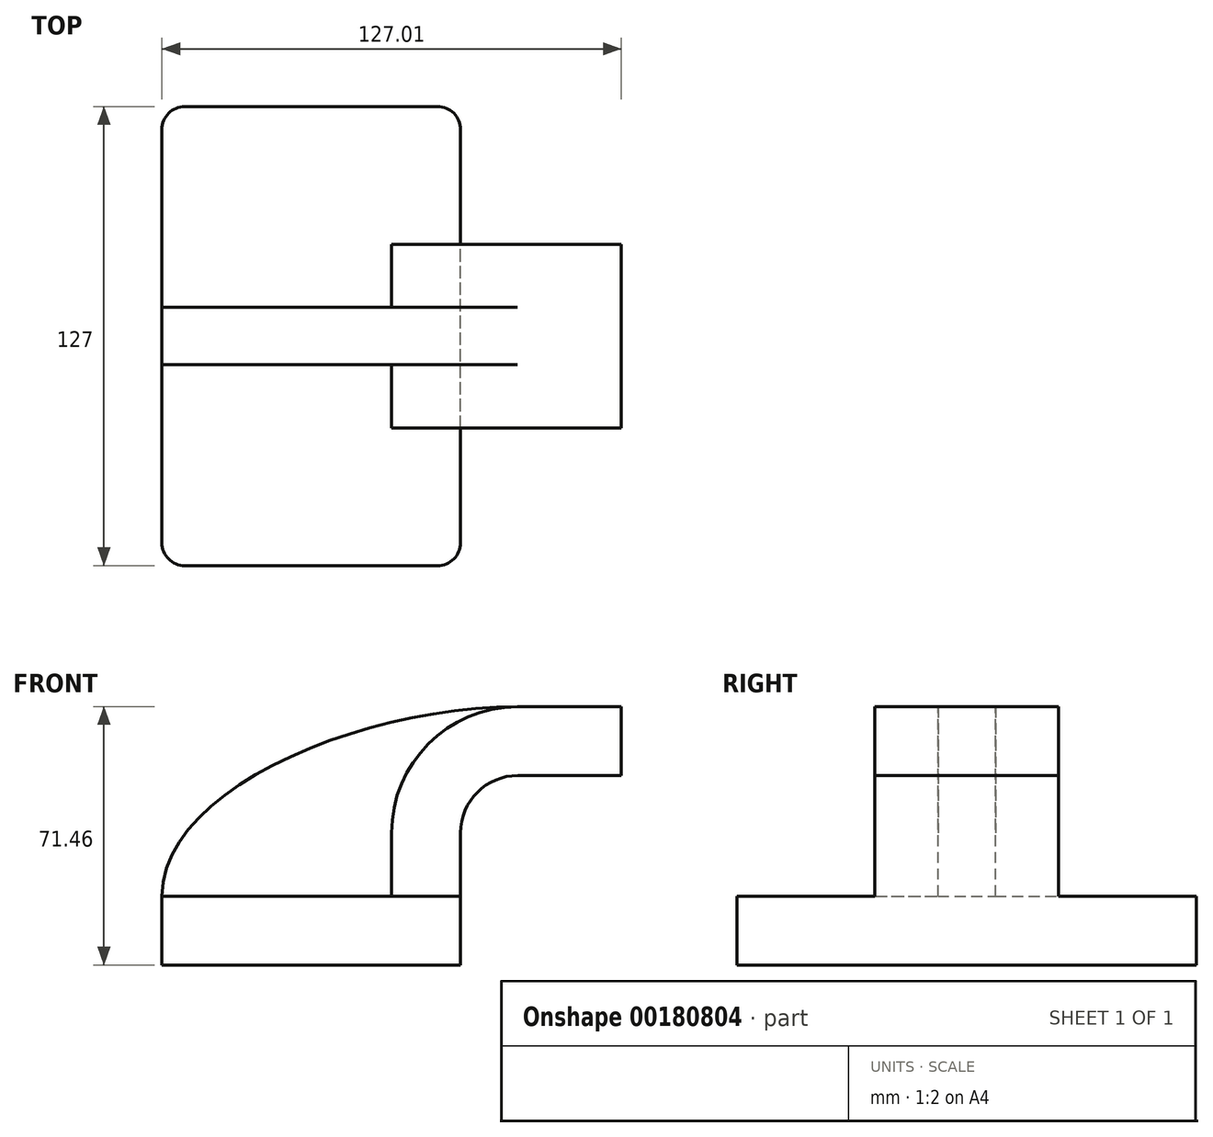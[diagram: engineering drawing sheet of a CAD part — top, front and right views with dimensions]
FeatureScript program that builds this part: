
annotation { "Feature Type Name" : "Feature", "Feature Type Description" : "" }
export const myFeature = defineFeature(function(context is Context, id is Id, definition is map)
    precondition{}
    {
        {
            var Q0;
            Q0=qCreatedBy(makeId("Front.planeOp"),FACE);
            var sketch = newSketch(context, id + "F0", { "sketchPlane" : qUnion([Q0])});
            skLineSegment(sketch, "E0.bottom", {"start": v(41.27, 9.53) * mm, "end": v(-41.28, 9.53) * mm});
            skLineSegment(sketch, "E0.top", {"start": v(41.28, -9.52) * mm, "end": v(-41.27, -9.52) * mm});
            skLineSegment(sketch, "E0.left", {"start": v(41.28, 9.53) * mm, "end": v(41.28, -9.52) * mm});
            skLineSegment(sketch, "E0.right", {"start": v(-41.28, 9.53) * mm, "end": v(-41.28, -9.52) * mm});
            skPoint(sketch, "E0.middle", {"position": v(0, 0) * mm});
            skLineSegment(sketch, "E1.bottom", {"start": v(111.12, 66.68) * mm, "end": v(60.33, 66.68) * mm});
            skLineSegment(sketch, "E1.top", {"start": v(111.12, 38.1) * mm, "end": v(60.33, 38.1) * mm});
            skLineSegment(sketch, "E1.left", {"start": v(111.12, 66.68) * mm, "end": v(111.12, 38.1) * mm});
            skLineSegment(sketch, "E1.right", {"start": v(60.32, 66.68) * mm, "end": v(60.33, 38.1) * mm});
            skPoint(sketch, "E1.middle", {"position": v(85.72, 52.39) * mm});
            skLineSegment(sketch, "E2", {"start": v(41.27, 9.53) * mm, "end": v(41.27, 27) * mm});
            skArc(sketch, "E3", {"start": v(41.27, 27) * mm, "mid": v(45.92, 38.23) * mm, "end": v(57.15, 42.88) * mm});
            skLineSegment(sketch, "E4", {"start": v(57.15, 42.88) * mm, "end": v(85.72, 42.88) * mm});
            skLineSegment(sketch, "E5.0", {"start": v(57.15, 61.93) * mm, "end": v(85.72, 61.93) * mm});
            skArc(sketch, "E5.1", {"start": v(22.22, 27) * mm, "mid": v(32.45, 51.7) * mm, "end": v(57.15, 61.93) * mm});
            skLineSegment(sketch, "E5.2", {"start": v(22.22, 9.53) * mm, "end": v(22.22, 27) * mm});
            skLineSegment(sketch, "E6", {"start": v(85.72, 42.88) * mm, "end": v(85.72, 66.68) * mm});
            skFitSpline(sketch, "E7", {"points": [v(-41.28, 9.52) * mm, v(57.15, 61.93) * mm], "startDerivative": vector(1.03, 90.32) * mm, "endDerivative": vector(129.37, 0.27) * mm});
            skSolve(sketch);
        }
        {
            var Q0;
            Q0=makeQuery(id+"F0.imprint","IMPRINT",FACE,{"disambiguationData":[TD([[makeQuery(id+"F0.imprint","IMPRINT",EDGE,{"derivedFrom":sQuery(id+"F0.wireOp",EDGE,"E0.top")}),-1.0]])]});
            extrude(context, id + "F1", {"entities" : qUnion([Q0]), "endBound" : BoundingType.SYMMETRIC, "depth" : 127 * mm});
        }
        {
            var Q0;
            {var subQ6=sQuery(id+"F0.wireOp",EDGE,"E2");Q0=makeQuery(id+"F0.imprint","IMPRINT",FACE,{"disambiguationData":[TD([[makeQuery(id+"F0.imprint","IMPRINT",EDGE,{"derivedFrom":subQ6}),1.0]])]});}
            var Q1;
            {var subQ0=sQuery(id+"F0.wireOp",EDGE,"E5.0");var subQ1=sQuery(id+"F0.wireOp",EDGE,"E1.right");var subQ2=makeQuery(id+"F0.imprint","INTERSECT",VERTEX,{"derivedFrom":[subQ1,subQ0]});Q1=makeQuery(id+"F0.imprint","IMPRINT",FACE,{"disambiguationData":[TD([[makeQuery(id+"F0.imprint","IMPRINT",EDGE,{"disambiguationData":[TD([[subQ2,-1.0]])],"derivedFrom":subQ1}),1.0]])]});}
            extrude(context, id + "F2", {"entities" : qUnion([Q0, Q1]), "operationType" : NewBodyOperationType.ADD, "endBound" : BoundingType.SYMMETRIC, "depth" : 50.8 * mm});
        }
        {
            var Q0;
            {var subQ3=sQuery(id+"F0.wireOp",EDGE,"E5.2");Q0=makeQuery(id+"F0.imprint","IMPRINT",FACE,{"disambiguationData":[TD([[makeQuery(id+"F0.imprint","IMPRINT",EDGE,{"derivedFrom":subQ3}),1.0]])]});}
            extrude(context, id + "F3", {"entities" : qUnion([Q0]), "operationType" : NewBodyOperationType.ADD, "endBound" : BoundingType.SYMMETRIC, "depth" : 15.88 * mm});
        }
        {
            var Q0;
            Q0=makeQuery(id+"F1.opExtrude","CAP_EDGE",EDGE,{"disambiguationData":[OSD([sQuery(id+"F0.wireOp",EDGE,"E0.right")])],"isStart":false});
            var Q1;
            Q1=makeQuery(id+"F1.opExtrude","CAP_EDGE",EDGE,{"disambiguationData":[OSD([sQuery(id+"F0.wireOp",EDGE,"E0.left")])],"isStart":false});
            var Q2;
            Q2=makeQuery(id+"F1.opExtrude","CAP_EDGE",EDGE,{"disambiguationData":[OSD([sQuery(id+"F0.wireOp",EDGE,"E0.left")])],"isStart":true});
            var Q3;
            Q3=makeQuery(id+"F1.opExtrude","CAP_EDGE",EDGE,{"disambiguationData":[OSD([sQuery(id+"F0.wireOp",EDGE,"E0.right")])],"isStart":true});
            fillet(context, id + "F4", {"entities" : qUnion([Q0, Q1, Q2, Q3]), "radius" : 6.35 * mm, "tangentPropagation" : true, "allowEdgeOverflow" : false});
        }
    });
